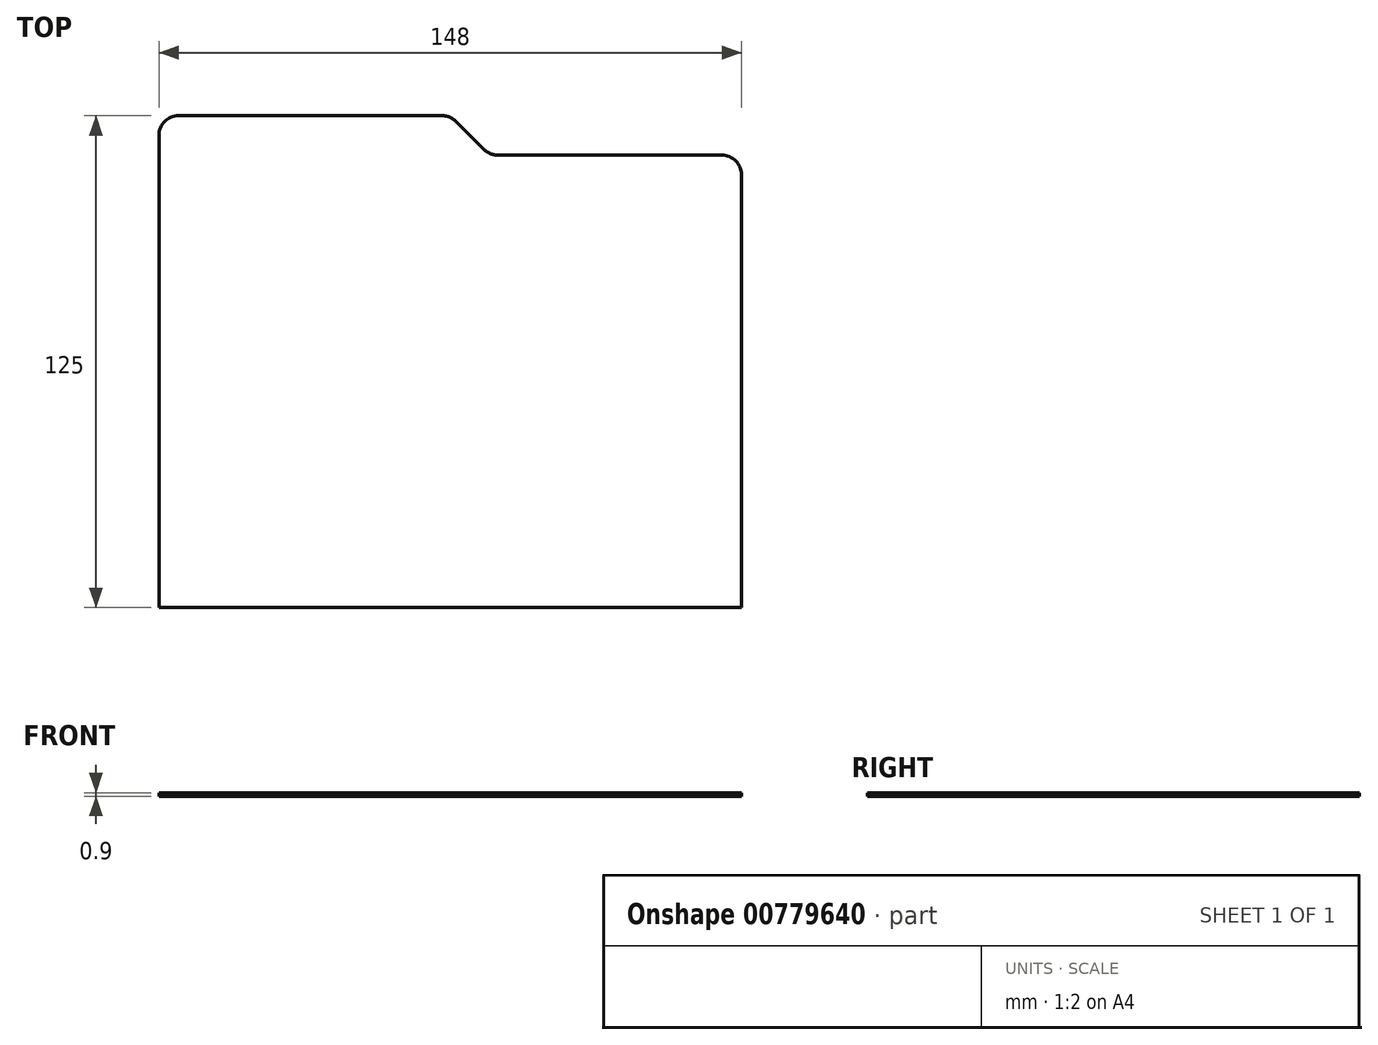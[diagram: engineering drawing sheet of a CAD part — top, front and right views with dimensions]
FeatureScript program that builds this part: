
annotation { "Feature Type Name" : "Feature", "Feature Type Description" : "" }
export const myFeature = defineFeature(function(context is Context, id is Id, definition is map)
    precondition{}
    {
        {
            var Q0;
            Q0=qCreatedBy(makeId("Top.planeOp"),FACE);
            var sketch = newSketch(context, id + "F0", { "sketchPlane" : qUnion([Q0])});
            skLineSegment(sketch, "E0.bottom", {"start": v(74, -62.5) * mm, "end": v(-74, -62.5) * mm});
            skLineSegment(sketch, "E0.top", {"start": v(0, 62.5) * mm, "end": v(-74, 62.5) * mm});
            skLineSegment(sketch, "E0.left", {"start": v(74, -62.5) * mm, "end": v(74, 52.5) * mm});
            skLineSegment(sketch, "E0.right", {"start": v(-74, -62.5) * mm, "end": v(-74, 62.5) * mm});
            skPoint(sketch, "E0.middle", {"position": v(0, 0) * mm});
            skLineSegment(sketch, "E1", {"start": v(0, 62.5) * mm, "end": v(10, 52.5) * mm});
            skLineSegment(sketch, "E2", {"start": v(10, 52.5) * mm, "end": v(74, 52.5) * mm});
            skPoint(sketch, "E3.orphan", {"position": v(74, 62.5) * mm});
            skSolve(sketch);
        }
        {
            var Q0;
            Q0=qSketchRegion(id+"F0",true);
            extrude(context, id + "F1", {"entities" : qUnion([Q0]), "depth" : 0.9 * mm});
        }
        {
            var Q0;
            Q0=makeQuery(id+"F1.opExtrude","SWEPT_EDGE",EDGE,{"disambiguationData":[OSD([sQuery(id+"F0.wireOp",EDGE,"E0.left"),sQuery(id+"F0.wireOp",EDGE,"E2")])]});
            var Q1;
            Q1=makeQuery(id+"F1.opExtrude","SWEPT_EDGE",EDGE,{"disambiguationData":[OSD([sQuery(id+"F0.wireOp",EDGE,"E0.top"),sQuery(id+"F0.wireOp",EDGE,"E1")])]});
            var Q2;
            Q2=makeQuery(id+"F1.opExtrude","SWEPT_EDGE",EDGE,{"disambiguationData":[OSD([sQuery(id+"F0.wireOp",EDGE,"E0.top"),sQuery(id+"F0.wireOp",EDGE,"E0.right")])]});
            var Q3;
            Q3=makeQuery(id+"F1.opExtrude","SWEPT_EDGE",EDGE,{"disambiguationData":[OSD([sQuery(id+"F0.wireOp",EDGE,"E1"),sQuery(id+"F0.wireOp",EDGE,"E2")])]});
            fillet(context, id + "F2", {"entities" : qUnion([Q0, Q1, Q2, Q3]), "radius" : 5 * mm, "tangentPropagation" : true, "allowEdgeOverflow" : false});
        }
    });
